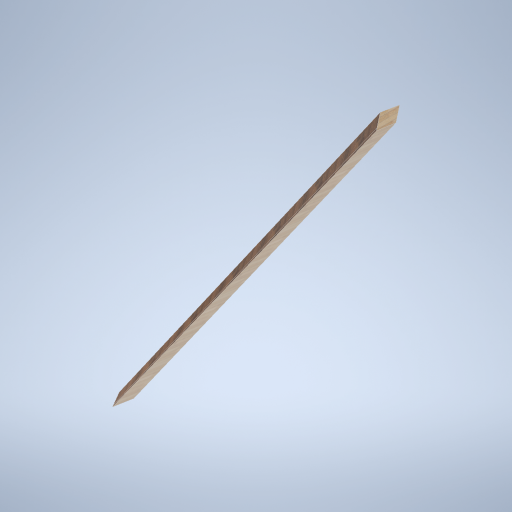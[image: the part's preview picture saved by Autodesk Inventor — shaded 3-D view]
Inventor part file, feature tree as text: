
AUTODESK INVENTOR PART (.ipt)
format: ipt  version: 2024.2 (Build 282272000, 272)  size: 294,912 bytes
history: native  units: mm
features: sketch x3, plane x2, loft x1
ambient origin geometry x8: Origin, YZ Plane, XZ Plane, XY Plane, X Axis, Y Axis, Z Axis, Center Point
bodies: Body1 (feature_tree)
feature tree (6):
  sketch  "Sketch13"  dims[d19=250.0mm d20=250.0mm]
  plane  "Work Plane9"
  loft  "Loft4"
  plane  "Work Plane8"
  sketch  "Sketch14"  dims[d21=8000.0mm]
  sketch  "Sketch15"  dims[d22=0.0mm d23=1791.0mm d24=40000.0mm d25=0.0mm d26=90.0deg d27=0.0mm d28=90.0deg]
